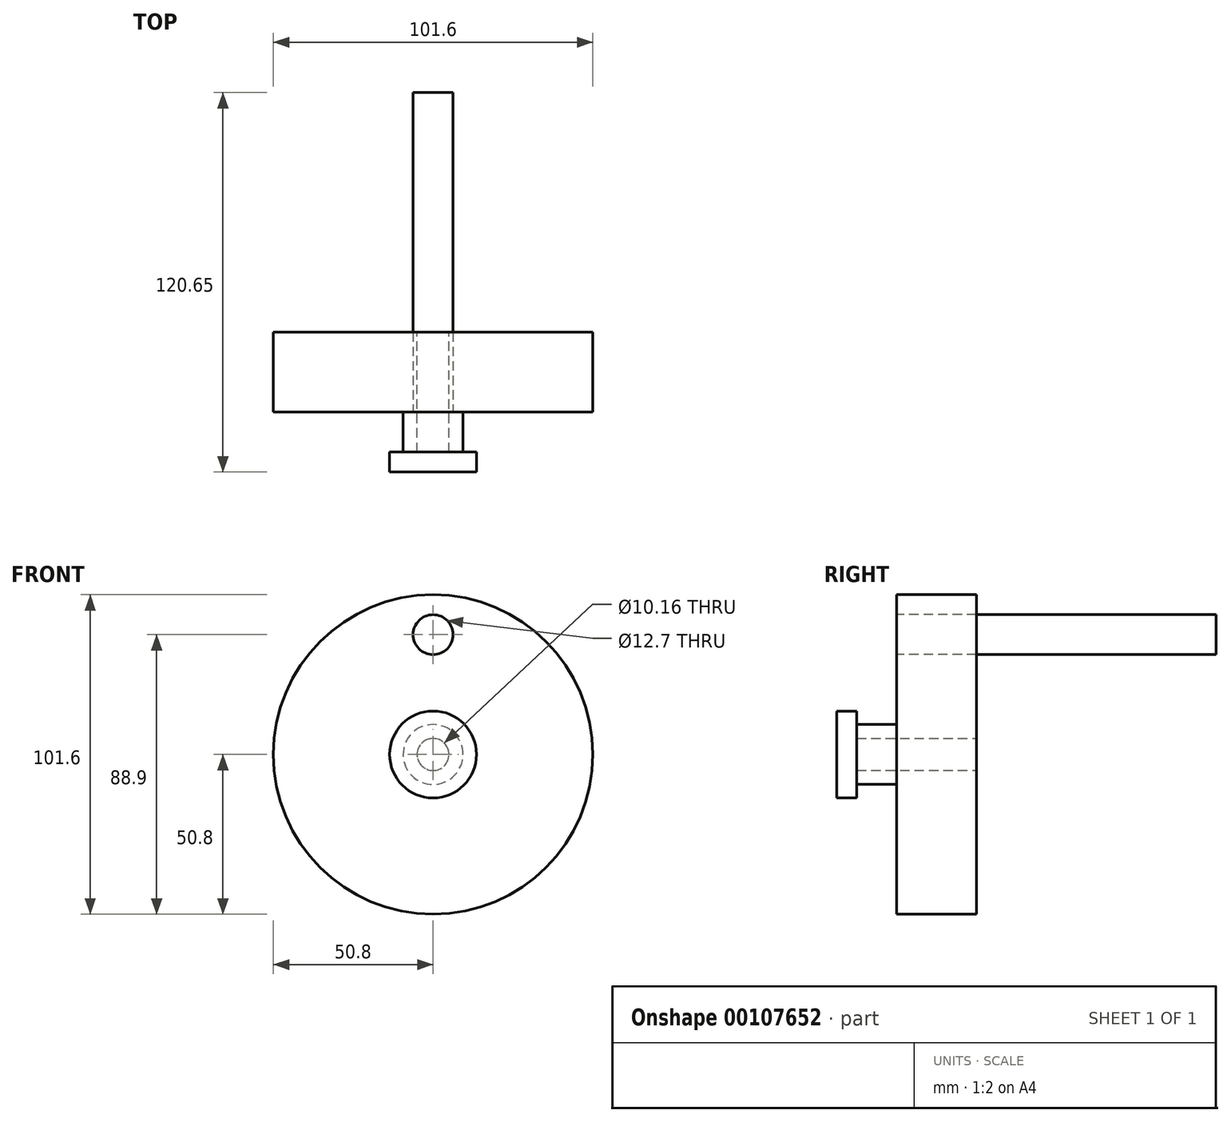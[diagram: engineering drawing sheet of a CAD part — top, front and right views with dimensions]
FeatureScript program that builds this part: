
annotation { "Feature Type Name" : "Feature", "Feature Type Description" : "" }
export const myFeature = defineFeature(function(context is Context, id is Id, definition is map)
    precondition{}
    {
        {
            var Q0;
            Q0=qCreatedBy(makeId("Front.planeOp"),FACE);
            var sketch = newSketch(context, id + "F0", { "sketchPlane" : qUnion([Q0])});
            skCircle(sketch, "E0", {"center": v(0, 0) * mm, "radius": 50.8 * mm});
            skCircle(sketch, "E1", {"center": v(0, 0) * mm, "radius": 25.4 * mm, "construction": true});
            skCircle(sketch, "E2", {"center": v(0, 25.4) * mm, "radius": 3.81 * mm, "construction": true});
            skSolve(sketch);
        }
        {
            var Q0;
            Q0 = qSketchRegion(id + "F0", true);
            extrude(context, id + "F1", {"entities" : qUnion([Q0]), "depth" : 25.4 * mm});
        }
        {
            var Q0;
            Q0=makeQuery(id+"F1.opExtrude","CAP_FACE",FACE,{"disambiguationData":[OSD([sQuery(id+"F0.wireOp",EDGE,"E0")])],"isStart":false});
            var sketch = newSketch(context, id + "F2", { "sketchPlane" : qUnion([Q0])});
            skCircle(sketch, "E3", {"center": v(0, 0) * mm, "radius": 9.53 * mm});
            skSolve(sketch);
        }
        {
            var Q0;
            Q0 = qSketchRegion(id + "F2", true);
            extrude(context, id + "F3", {"entities" : qUnion([Q0]), "operationType" : NewBodyOperationType.ADD, "depth" : 12.7 * mm});
        }
        {
            var Q0;
            Q0=makeQuery(id+"F1.opExtrude","CAP_FACE",FACE,{"disambiguationData":[OSD([sQuery(id+"F0.wireOp",EDGE,"E0")])],"isStart":true});
            var sketch = newSketch(context, id + "F4", { "sketchPlane" : qUnion([Q0])});
            skCircle(sketch, "E4", {"center": v(0, 0) * mm, "radius": 5.08 * mm});
            skSolve(sketch);
        }
        {
            var Q0;
            Q0 = qSketchRegion(id + "F4", true);
            extrude(context, id + "F5", {"entities" : qUnion([Q0]), "operationType" : NewBodyOperationType.REMOVE, "oppositeDirection" : true, "depth" : 50.8 * mm});
        }
        {
            var Q0;
            Q0=makeQuery(id+"F1.opExtrude","CAP_FACE",FACE,{"disambiguationData":[OSD([sQuery(id+"F0.wireOp",EDGE,"E0")])],"isStart":false});
            var sketch = newSketch(context, id + "F6", { "sketchPlane" : qUnion([Q0])});
            skCircle(sketch, "E5", {"center": v(0, 38.1) * mm, "radius": 6.35 * mm});
            skSolve(sketch);
        }
        {
            var Q0;
            Q0 = qSketchRegion(id + "F6", true);
            extrude(context, id + "F7", {"entities" : qUnion([Q0]), "operationType" : NewBodyOperationType.REMOVE, "oppositeDirection" : true, "depth" : 25.4 * mm});
        }
        {
            var Q0;
            Q0 = qSketchRegion(id + "F6", true);
            extrude(context, id + "F8", {"entities" : qUnion([Q0]), "oppositeDirection" : true, "depth" : 101.6 * mm});
        }
        {
            var Q0;
            Q0=makeQuery(id+"F3.opExtrude","CAP_FACE",FACE,{"disambiguationData":[OSD([sQuery(id+"F2.wireOp",EDGE,"E3")])],"isStart":false});
            var sketch = newSketch(context, id + "F9", { "sketchPlane" : qUnion([Q0])});
            skCircle(sketch, "E6", {"center": v(0, 0) * mm, "radius": 13.81 * mm});
            skSolve(sketch);
        }
        {
            var Q0;
            Q0 = qSketchRegion(id + "F9", true);
            extrude(context, id + "F10", {"entities" : qUnion([Q0]), "depth" : 6.35 * mm});
        }
    });
